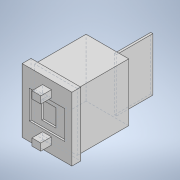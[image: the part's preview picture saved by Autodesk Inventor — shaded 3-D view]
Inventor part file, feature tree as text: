
AUTODESK INVENTOR PART (.ipt)
format: ipt  version: 2021 (Build 250183000, 183)  size: 150,528 bytes
history: native  units: mm
features: extrude x6, sketch x6, projected_geometry x1
ambient origin geometry x8: Origin, YZ Plane, XZ Plane, XY Plane, X Axis, Y Axis, Z Axis, Center Point
bodies: Solid1 (feature_tree)
feature tree (13):
  extrude  "Extrusion1"  Depth=16.3mm
  extrude  "Extrusion2"  Depth=14.0mm
  extrude  "Extrusion3"  Depth=2.5mm TaperAngle=0.0deg
  extrude  "Extrusion4"  Depth=8.0mm
  extrude  "Extrusion5"  Depth=4.0mm
  extrude  "Extrusion6"  Depth=0.5mm TaperAngle=0.0deg
  sketch  "Sketch1"  dims[d0=12.0mm d1=16.3mm]
  sketch  "Sketch2"  dims[d2=14.5mm d3=0.0mm d4=14.0mm]
  projected_geometry  "Projected Loop1"
  sketch  "Sketch3"  dims[d5=18.0mm d6=2.5mm d7=0.0mm]
  sketch  "Sketch4"  dims[d8=10.0mm d9=8.0mm]
  sketch  "Sketch5"  dims[d10=0.5mm d11=0.0mm d12=4.0mm]
  sketch  "Sketch6"  dims[d13=5.0mm d14=0.5mm d15=0.0mm d16=2.5mm d17=2.0mm d18=13.5mm d19=6.75mm d20=3.0mm d21=0.0mm d22=15.0mm d23=3.4mm d24=0.6mm d25=10.2mm d26=0.0mm]
